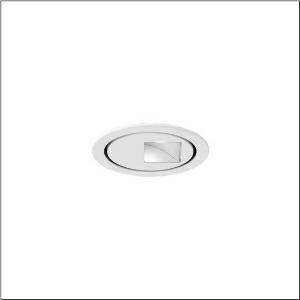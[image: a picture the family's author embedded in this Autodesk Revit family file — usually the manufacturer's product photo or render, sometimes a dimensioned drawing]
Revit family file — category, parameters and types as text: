
# Revit family: lunis_11_micro_round_51dj11cd1wg21
name_source: partatom
category: Lighting Fixtures
units: mm (PartAtom-declared; Revit-internal decimal feet)

## family parameters
Cut with Voids When Loaded = No
Host = Face
Light Source = No
Part Type = Normal
Room Calculation Point = No
Round Connector Dimension = Use Diameter
Shared = No

## types (1)
- Lunis 11 micro round (1 x LED 4000K / CRI = 80 (unbekannt), 1400 lm, 4000K)
    Apparent Load = 20 VA
    CIE Flux Codes = 42 75 96 100 100
    Color Rendering = 80
    Color Temperature = 4000K
    Default Elevation = 1800 mm
    Description = Lunis 11 micro round, downlight, light control with wallwasher, of highly reflective aluminium, highly specular, light emission: direct distribution, LED rated luminous flux: 1.400lm, light colour: 840, with terminal, 5-pole, mains connection: 220..230V, AC, 50/60Hz, LED module, of aluminium, highly specular, white, diameter: 114mm, clamping range: 1..40mm, recessing ring, of plastic, traffic white (RAL 9016), protection rating (complete): IP20, insulation class (complete): insulation class II (safety insulation), certification: CE, permissible ambient temperature for indoor applications: 0..+35°C, packaging unit: 1 piece
    Height = 0 mm  [stored 0 ft]
    Lamp = 1 x LED 4000K / CRI >= 80 (unbekannt)
    Lamp Light Flux = 1400 lm
    Lamp count = 1
    Length = 114 mm
    Luminous efficacy = 71 lm/W
    Manufacturer = Siteco
    ModVariant = No
    Model = 51DJ11CD1WG21
    Mounting Place = Ceiling
    Mounting Type = Recessed
    Number of Poles = 1
    OnlyDefault = Yes
    Power Factor = 1
    Product Name = Lunis 11 micro round
    Product group = downlight
    ProductGroupID = 401
    Protection Class = Protection class II
    Protection Degree = IP 20
    RLX_Detail_Level = 1
    RLX_Emergency_Light_Flux = 0 lm
    RLX_Emergency_Type = 0
    RLX_Emergency_Type_DB = No
    RlxData = <blob elided: 40289 chars, md5=eeed79aa>
    Socket = socket
    Standby Power = 0 W
    System Light Flux = 1400 lm
    System Power = 20 W
    Type Comments = Product without accessories
    Type Image = l_1004773.jpg
    URL = http://relux.com
    VarID = ---
    Voltage = 0 V
    Weight = 0.00 kg
    Width = 114 mm

note: [stored X ft] marks values corroborated as IEEE doubles in the binary element streams (Revit-internal decimal feet)

## geometry (parser evidence)
native form markers: Blend x4, Sweep x10
no freeform markers — native parametric forms only
